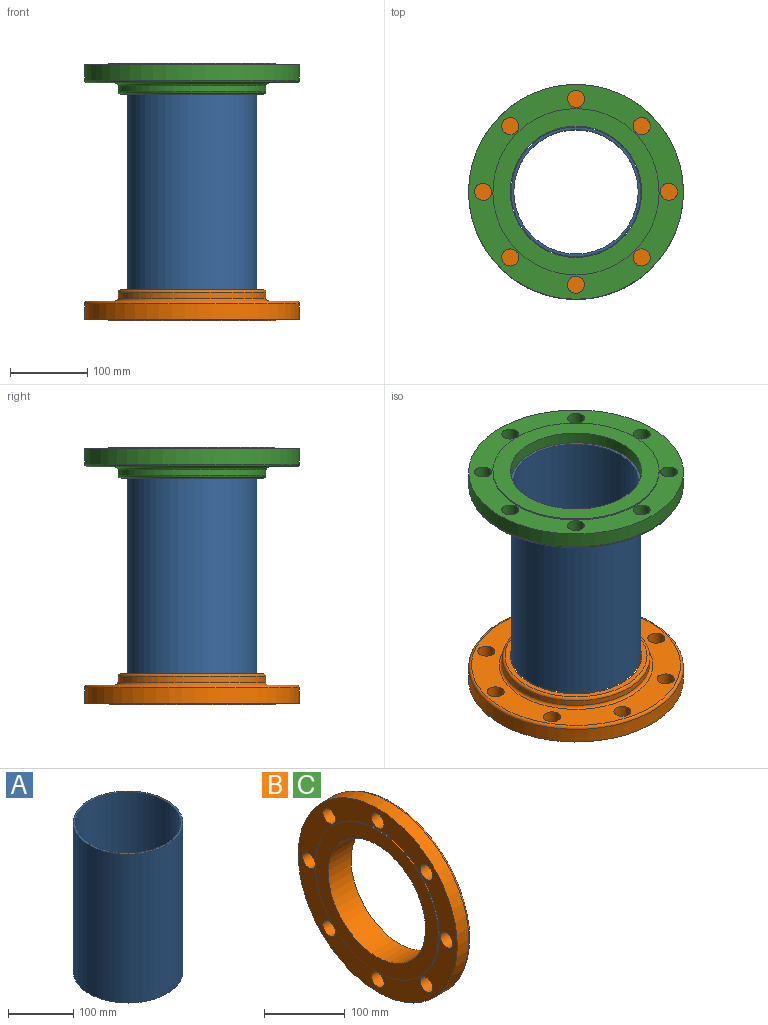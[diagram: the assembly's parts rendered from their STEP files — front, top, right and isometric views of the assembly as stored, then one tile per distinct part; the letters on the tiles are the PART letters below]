
ASSEMBLY  parts=3 mates=1
PART A: 4 faces, bbox 168.3x168.3x279.4 mm
  f0: cylinder r=80.73mm len=279.4mm, axis (0,0,1), area 141730.1mm2, adj f1,f2
  f1: plane 168.28x168.28mm, normal (0,0,-1), area 1762.9mm2, adj f0,f3
  f2: plane 168.28x168.28mm, normal (0,0,1), area 1762.9mm2, adj f0,f3
  f3: cylinder r=84.14mm len=279.4mm, axis (0,0,1), area 147705.2mm2, adj f1,f2
PART B: 19 faces, bbox 40x302x302 mm
  f0: torus R=92.25mm, axis (1,0,0), area 3502.5mm2, adj f1,f17
  f1: cylinder r=96mm len=192mm, axis (1,0,0), area 4282.8mm2, adj f0,f2
  f2: torus R=99.75mm, axis (1,0,0), area 3603.4mm2, adj f1,f16
  f3: torus R=135.75mm, axis (1,0,0), area 5112.4mm2, adj f4,f16
  f4: cylinder r=139.5mm len=279mm, axis (1,0,0), area 17574mm2, adj f3,f15
  f5: cylinder r=107.95mm len=215.9mm, axis (1,0,0), area 1085.2mm2, adj f15,f18
  f6: cylinder r=11.1mm len=23.8mm, axis (1,0,0), area 1659.9mm2, adj f15,f16
  f7: cylinder r=11.1mm len=23.8mm, axis (1,0,0), area 1659.9mm2, adj f15,f16
  f8: cylinder r=11.1mm len=23.8mm, axis (1,0,0), area 1659.9mm2, adj f15,f16
  f9: cylinder r=11.1mm len=23.8mm, axis (1,0,0), area 1659.9mm2, adj f15,f16
  f10: cylinder r=11.1mm len=23.8mm, axis (1,0,0), area 1659.9mm2, adj f15,f16
  f11: cylinder r=11.1mm len=23.8mm, axis (1,0,0), area 1659.9mm2, adj f15,f16
  f12: cylinder r=11.1mm len=23.8mm, axis (1,0,0), area 1659.9mm2, adj f15,f16
  f13: cylinder r=11.1mm len=23.8mm, axis (1,0,0), area 1659.9mm2, adj f15,f16
  f14: cylinder r=85.35mm len=170.7mm, axis (1,0,0), area 21450.8mm2, adj f17,f18
  f15: plane 279x279mm, normal (-1,0,0), area 21430mm2, adj f4,f5,f6,f7,f8,f9,f10,f11
  f16: plane 271.5x271.5mm, normal (1,0,0), area 23538mm2, adj f2,f3,f6,f7,f8,f9,f10,f11
  f17: plane 184.5x184.5mm, normal (1,0,0), area 3849.9mm2, adj f0,f14
  f18: plane 215.9x215.9mm, normal (-1,0,0), area 13724.3mm2, adj f5,f14
PART C: same geometry as B
PLACE A rot(axis=(0,0,1),90deg) t=(49.76,-86.84,71.51)mm
PLACE B rot(axis=(-0.45,-0.77,-0.45),104.5deg) t=(49.76,-86.84,31.51)mm
PLACE C rot(axis=(0,1,0),90deg) t=(49.76,-86.84,365.51)mm
MATE revolute C.f0 <-> A.f0  axis (0,0,-1) through (49.76,-86.84,325.51)mm
